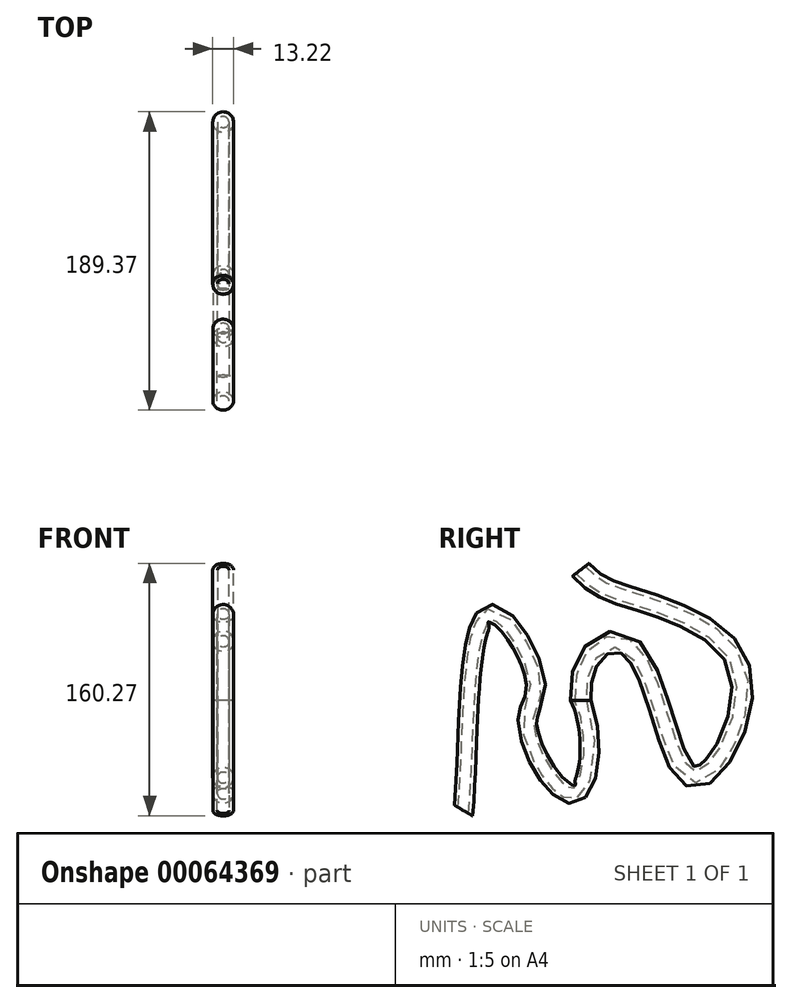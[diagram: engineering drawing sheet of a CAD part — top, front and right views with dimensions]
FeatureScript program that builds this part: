
annotation { "Feature Type Name" : "Feature", "Feature Type Description" : "" }
export const myFeature = defineFeature(function(context is Context, id is Id, definition is map)
    precondition{}
    {
        {
            var Q0;
            Q0=qCreatedBy(makeId("Top.planeOp"),FACE);
            var sketch = newSketch(context, id + "F0", { "sketchPlane" : qUnion([Q0])});
            skCircle(sketch, "E0", {"center": v(0, 0) * mm, "radius": 6.57 * mm});
            skCircle(sketch, "E1", {"center": v(0, 0) * mm, "radius": 3.81 * mm});
            skSolve(sketch);
        }
        {
            var Q0;
            Q0=qCreatedBy(makeId("Right.planeOp"),FACE);
            var sketch = newSketch(context, id + "F1", { "sketchPlane" : qUnion([Q0])});
            skPoint(sketch, "E2.start.orphan", {"position": v(35.28, 28.95) * mm});
            skFitSpline(sketch, "E3", {"points": [v(0, 0) * mm, v(-4.96, -59.03) * mm, v(-33.67, -16.47) * mm, v(-28.73, 11.5) * mm, v(-58.09, 54.37) * mm, v(-74.5, -69.92) * mm], "startDerivative": vector(145.13, -323.6) * mm, "endDerivative": vector(-38.4, -337.83) * mm});
            skPoint(sketch, "E4.end.orphan", {"position": v(0, 28.95) * mm});
            skSolve(sketch);
        }
        {
            var Q0;
            Q0 = qSketchRegion(id + "F0", true);
            var Q1;
            Q1 = qConstructionFilter(qBodyType(qCreatedBy(id + "F1" ,EDGE), BodyType.WIRE), ConstructionObject.NO);
            sweep(context, id + "F2", {"profiles" : qUnion([Q0]), "path" : qUnion([Q1])});
        }
        {
            var Q0;
            Q0=qCreatedBy(makeId("Top.planeOp"),FACE);
            var sketch = newSketch(context, id + "F3", { "sketchPlane" : qUnion([Q0])});
            skCircle(sketch, "E5", {"center": v(0, 0) * mm, "radius": 6.61 * mm});
            skCircle(sketch, "E6", {"center": v(0, 0) * mm, "radius": 3.66 * mm});
            skSolve(sketch);
        }
        {
            var Q0;
            Q0=qCreatedBy(makeId("Right.planeOp"),FACE);
            var sketch = newSketch(context, id + "F4", { "sketchPlane" : qUnion([Q0])});
            skFitSpline(sketch, "E7", {"points": [v(0, 0) * mm, v(31.16, 34.22) * mm, v(71.02, -48.65) * mm, v(100.91, 20.37) * mm, v(21.07, 68.84) * mm, v(0, 82.96) * mm], "startDerivative": vector(-47.4, 518.95) * mm, "endDerivative": vector(-134.62, 145.43) * mm});
            skLineSegment(sketch, "E8", {"start": v(6.26, 76.82) * mm, "end": v(6.26, 76.82) * mm});
            skSolve(sketch);
        }
        {
            var Q0;
            Q0 = qSketchRegion(id + "F3", true);
            var Q1;
            Q1 = qConstructionFilter(qBodyType(qCreatedBy(id + "F4" ,EDGE), BodyType.WIRE), ConstructionObject.NO);
            sweep(context, id + "F5", {"operationType" : NewBodyOperationType.ADD, "profiles" : qUnion([Q0]), "path" : qUnion([Q1])});
        }
    });
